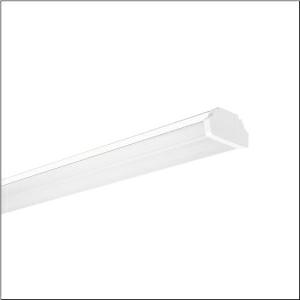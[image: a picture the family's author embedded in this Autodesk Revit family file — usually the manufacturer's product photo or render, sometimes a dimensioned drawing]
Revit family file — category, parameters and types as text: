
# Revit family: dus_r__31_gen_2_53bd812cv4dxd2_dd4f
name_source: partatom
category: Lighting Fixtures
units: mm (PartAtom-declared; Revit-internal decimal feet)

## family parameters
Cut with Voids When Loaded = No
Host = Face
Light Source = No
Part Type = Normal
Room Calculation Point = No
Round Connector Dimension = Use Diameter
Shared = No

## types (1)
- --- (1 x LED, 13040 lm, 68.5 W, 4000K)
    Apparent Load = 69 VA
    CIE Flux Codes = 47 80 95 93 100
    Color Rendering = 80
    Color Temperature = 4000K
    Default Elevation = 1800 mm
    Description = DUS® 31 Gen.2, luminaire insert, of sheet steel, coil coated, white, length: 1.535mm, width: 81mm, height: 90mm, 5x system unit, system units: 307mm, LED rated luminous flux: 13.040lm, light colour: 840, control gear: ON/OFF Multilumen, CLOi, with plug, 3-pole, with phase selection, mains connection: 220..240V, AC, 50/60Hz, start of lifetime: 69W, end of service life: 82W, through-wiring accessed according to module size, primary optical cover: cover, of PMMA, light emission: direct distribution, primary light characteristic: symmetric, protection rating (complete): IP20, protection rating (LED compartment): IP50, insulation class (complete): insulation class I (protective earthing), certification: CE, ENEC, VDE, UKCA, impact resistance: IK03, permissible ambient temperature for indoor applications: -35..+35°C, corresponds to IFS (International Featured Standards) requirements for safety and quality in the food industry, reducing of maximum allowable ambient temperature of 5°C with ceiling mounting, packaging unit: 1 piece
    Height = 95 mm
    Lamp = 1 x LED
    Lamp Light Flux = 13040 lm
    Lamp Power = 68.5 W
    Lamp count = 1
    Length = 1535 mm
    Luminous efficacy = 190 lm/W
    Manufacturer = Siteco
    ModVariant = No
    Model = 53BD812CV4DXD2
    Mounting Place = Ceiling
    Mounting Type = Pendant
    Number of Poles = 1
    OnlyDefault = Yes
    Power Factor = 1
    Product Name = DUS® 31 Gen.2
    Product group = luminaire insert
    ProductGroupID = 901
    Protection Class = Protection class I
    Protection Degree = IP 20
    RLX_Detail_Level = 1
    RLX_Emergency_Light_Flux = 0 lm
    RLX_Emergency_Type = 0
    RLX_Emergency_Type_DB = No
    RlxData = <blob elided: 29893 chars, md5=7f042daa>
    Socket = socket
    Standby Power = 0 W
    System Light Flux = 13040 lm
    System Power = 69 W
    Type Comments = factory setting: luminous flux: 100 % | (A | C | E) | 161 mA
    Type Image = l_1319596.jpg
    URL = http://relux.com
    VarID = @adj_010003
    Voltage = 0 V
    Weight = 0.00 kg
    Width = 81 mm

## geometry (parser evidence)
native form markers: Blend x4, Sweep x13
no freeform markers — native parametric forms only
